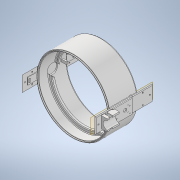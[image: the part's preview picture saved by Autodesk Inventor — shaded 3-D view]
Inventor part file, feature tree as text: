
AUTODESK INVENTOR PART (.ipt)
format: ipt  version: 2020.2 (Build 242310000, 310)  size: 672,256 bytes
history: native  units: mm
features: reference x25, extrude x24, sketch x24, other x7, plane x5, chamfer x2, pattern_circular x2, mirror x1
ambient origin geometry x8: Origin, YZ Plane, XZ Plane, XY Plane, X Axis, Y Axis, Z Axis, Center Point
bodies: Solid1 (feature_tree)
feature tree (90):
  extrude  "Extrusion1"  Depth=205.0mm
  extrude  "Extrusion2"  Depth=208.633333mm
  plane  "Work Plane4"
  extrude  "Extrusion3"  Depth=3.0mm TaperAngle=0.0deg
  extrude  "Extrusion4"  Depth=45.0mm
  extrude  "Extrusion6"  TaperAngle=0.0deg  [1 undecoded]
  extrude  "Extrusion8"  Depth=0.1mm
  chamfer  "Chamfer1"  Distance=20.0mm Angle=360.0deg
  pattern_circular  "Circular Pattern1"  Count=8  [1 undecoded]
  mirror  "Mirror1"
  plane  "Work Plane6"
  plane  "Work Plane8"
  extrude  "Extrusion15"  Depth=20.5mm
  extrude  "Extrusion16"  Depth=1.0mm
  extrude  "Extrusion17"  Depth=8.0mm
  extrude  "Extrusion20"  Depth=20.0mm TaperAngle=0.0deg
  chamfer  "Chamfer2"  Distance=5.0mm
  pattern_circular  "Circular Pattern2"  Count=2 Angle=360.0deg
  extrude  "Extrusion19"  Depth=191.666667mm
  extrude  "Extrusion21"  Depth=3.0mm TaperAngle=0.0deg
  extrude  "Extrusion22"  Depth=20.0mm
  extrude  "Extrusion23"  Depth=10.0mm
  extrude  "Extrusion24"  Depth=10.0mm
  plane  "Work Plane10"
  extrude  "Extrusion25"  Depth=10.0mm
  extrude  "Extrusion26"  Depth=10.0mm
  extrude  "Extrusion27"  TaperAngle=0.0deg  [1 undecoded]
  extrude  "Extrusion28"  TaperAngle=0.0deg  [1 undecoded]
  extrude  "Extrusion29"  TaperAngle=0.0deg  [1 undecoded]
  extrude  "Extrusion30"  Depth=10.0mm
  extrude  "Extrusion31"  Depth=10.0mm TaperAngle=0.0deg
  extrude  "Extrusion32"  Depth=10.0mm TaperAngle=0.0deg
  extrude  "Extrusion33"  Depth=10.0mm TaperAngle=0.0deg
  sketch  "Sketch1"  dims[d0=215.0mm d1=205.0mm]
  sketch  "Sketch2"  dims[d2=40.0mm d3=0.0mm d4=208.633333mm]
  plane  "Work Plane3"
  sketch  "Sketch4"  dims[d5=211.366667mm d6=3.0mm d7=0.0mm]
  sketch  "Sketch5"  dims[d8=45.0mm d9=45.0mm]
  reference  "Reference1"
  sketch  "Sketch6"  dims[d10=3.0mm d11=0.0mm d12=0.0mm]
  sketch  "Sketch8"  dims[d13=2.0mm d14=0.0mm d17=0.1mm]
  reference  "Reference7"
  reference  "Reference8"
  reference  "Reference9"
  reference  "Reference10"
  sketch  "Sketch16"  dims[d18=1.9mm]
  sketch  "Sketch17"  dims[d19=0.0mm d23=20.0mm d24=360.0deg]
  reference  "Reference12"
  reference  "Reference13"
  sketch  "Sketch18"  dims[d26=0.1mm]
  sketch  "Sketch20"  dims[d27=1.0mm d28=0.0mm]
  sketch  "Sketch21"  dims[d29=2.0mm d30=2.0mm d31=45.0deg]
  sketch  "Sketch22"  dims[d67=30.2mm]
  sketch  "Sketch23"  dims[d68=41.0mm d69=80.0mm]
  reference  "Reference14"
  reference  "Reference15"
  sketch  "Sketch24"  dims[d70=40.0mm d71=20.5mm]
  sketch  "Sketch25"  dims[d72=215.0mm d73=0.0mm d74=1.0mm]
  reference  "Reference16"
  reference  "Reference17"
  sketch  "Sketch26"  dims[d75=4.0mm d76=8.0mm]
  reference  "Reference18"
  reference  "Reference19"
  sketch  "Sketch27"  dims[d77=26.0mm d78=20.0mm d79=0.0mm]
  reference  "Reference20"
  reference  "Reference21"
  sketch  "Sketch28"  dims[d80=10.0mm d83=5.0mm d84=0.0mm]
  sketch  "Sketch29"  dims[d85=0.0mm]
  reference  "Reference22"
  reference  "Reference23"
  reference  "Reference24"
  reference  "Reference25"
  sketch  "Sketch30"  dims[d86=2.5mm d87=0.0mm d97=20.0mm d98=360.0deg]
  reference  "Reference26"
  reference  "Reference27"
  sketch  "Sketch31"  dims[d100=215.0mm d101=0.0mm d102=191.666667mm]
  sketch  "Sketch32"  dims[d103=198.333333mm d104=3.0mm d105=0.0mm]
  reference  "Reference28"
  reference  "Reference29"
  sketch  "Sketch33"  dims[d106=2.0mm d107=2.0mm d108=45.0deg d110=20.0mm]
  reference  "Reference30"
  sketch  "Sketch34"  dims[d111=72.5mm d112=0.0mm d114=0.4mm d115=6.0mm d116=6.8mm d117=6.8mm d118=0.0mm d119=0.0mm d120=0.0mm d121=6.0mm d122=4.0mm d123=0.0mm d124=7.5mm d125=0.0mm d126=3.0mm d127=0.0mm d128=2.0mm d129=2.0mm d130=6.0mm d131=0.0mm d132=-7.0mm d133=16.0mm d134=8.0mm d135=0.5mm d136=40.0mm d137=30.2mm d138=3.0mm d139=22.0mm d140=0.0mm d141=2.0mm d142=2.0mm d143=10.0mm d144=0.0mm d145=5.0mm d146=5.0mm d147=4.0mm d148=0.0mm d149=100.0mm d150=0.0mm d151=57.0mm d153=10.0mm d154=3.0mm d155=0.0mm d156=10.0mm d157=0.0mm d158=3.0mm d159=3.0mm d160=5.0mm d161=0.0mm d162=1.5mm d163=0.0mm d164=2.0mm d165=2.0mm d166=5.0mm d167=0.0mm d168=5.0mm d169=17.0mm d170=0.0mm d171=0.4mm d172=17.5mm d173=0.0mm d174=3.0mm d175=3.0mm d88=0.872665mm]
  reference  "Reference31"
  other  "<userpath>\OneDrive\Apps\0011_VentControlValve\Assembly.iam"
  other  "Assembly.iam"
  other  "Base:1"
  other  "Butterfly Valve:1"
  other  "limitSwitch:2"
  other  "limitSwitch:1"
  other  "motor+Gearbox:1"
note: 5 required parameter values undecoded (feature->parameter linkage not recoverable at this tier; creation-order binding heuristic only, values carry confidence <= 0.55)
